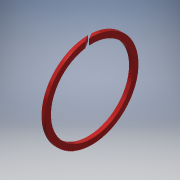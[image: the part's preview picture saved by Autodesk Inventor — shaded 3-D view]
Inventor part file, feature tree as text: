
AUTODESK INVENTOR PART (.ipt)
format: ipt  version: 2018 (Build 220112000, 112)  size: 159,232 bytes
history: native  units: mm
features: extrude x2, sketch x2, fillet x1, direct_edit x1, projected_geometry x1, move_body x1
ambient origin geometry x8: Origin, YZ Plane, XZ Plane, XY Plane, X Axis, Y Axis, Z Axis, Center Point
bodies: Solid1 (feature_tree)
feature tree (8):
  extrude  "Extrusion1"  Depth=21.0mm
  extrude  "Extrusion2"  Depth=0.5mm
  fillet  "Fillet1"  [1 undecoded]
  direct_edit  "Direct Edit1"
  sketch  "Sketch1"  dims[d0=24.0mm d1=21.0mm]
  sketch  "Sketch2"  dims[d2=1.0mm d3=0.0mm d4=12.73mm d5=30.0deg d6=1.0mm d7=17.0mm d8=0.0mm d9=0.15mm d10=0.0mm d11=0.0mm d12=0.5mm]
  projected_geometry  "Project Cut Edges1"
  move_body  "Move1"
note: 1 required parameter value undecoded (feature->parameter linkage not recoverable at this tier; creation-order binding heuristic only, values carry confidence <= 0.55)
